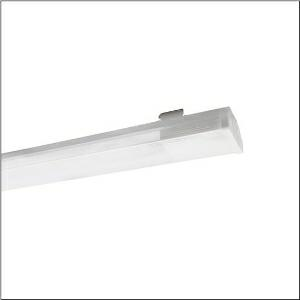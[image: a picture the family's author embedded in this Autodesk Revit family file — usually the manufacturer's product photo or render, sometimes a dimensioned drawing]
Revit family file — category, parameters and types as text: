
# Revit family: modario_r__31_gen_2_53bm8117u4gxc2_3746
name_source: partatom
category: Lighting Fixtures
units: mm (PartAtom-declared; Revit-internal decimal feet)

## family parameters
Cut with Voids When Loaded = No
Host = Face
Light Source = No
Part Type = Normal
Room Calculation Point = No
Round Connector Dimension = Use Diameter
Shared = No

## types (1)
- Modario® 31 Gen.2 (1 x LED, 16360 lm, 90.4 W, 4000K)
    Apparent Load = 90 VA
    CIE Flux Codes = 50 78 94 90 100
    Color Rendering = 80
    Color Temperature = 4000K
    Default Elevation = 1800 mm
    Description = Modario® 31 Gen.2, luminaire insert, of sheet steel, coil coated, white, length: 2.392mm, width: 81mm, height: 82mm, 8x system unit, system units: 299mm, LED rated luminous flux: 16.360lm, light colour: 840, control gear: ON/OFF, with plug, 3-pole, with phase selection, mains connection: 220..240V, AC, 50/60Hz, rated input power: 90W, through-wiring accessed according to module size, primary optical cover: cover, of PMMA, light emission: direct distribution, primary light characteristic: symmetric, protection rating (complete): IP20, protection rating (LED compartment): IP50, insulation class (complete): insulation class I (protective earthing), certification: CE, ENEC, VDE, UKCA, impact resistance: IK03, permissible ambient temperature for indoor applications: -40..+40°C, corresponds to IFS (International Featured Standards) requirements for safety and quality in the food industry, reducing of maximum allowable ambient temperature of 5°C with ceiling mounting, packaging unit: 1 piece
    Height = 92 mm
    Lamp = 1 x LED
    Lamp Light Flux = 16360 lm
    Lamp Power = 90.4 W
    Lamp count = 1
    Length = 2392 mm
    Luminous efficacy = 181 lm/W
    Manufacturer = Siteco
    ModVariant = No
    Model = 53BM8117U4GXC2
    Mounting Place = Ceiling
    Mounting Type = Pendant
    Number of Poles = 1
    OnlyDefault = Yes
    Power Factor = 1
    Product Name = Modario® 31 Gen.2
    Product group = luminaire insert | ceiling pendant
    ProductGroupID = 902
    Protection Class = Protection class I
    Protection Degree = IP 20
    RLX_Detail_Level = 1
    RLX_Emergency_Light_Flux = 0 lm
    RLX_Emergency_Type = 0
    RLX_Emergency_Type_DB = No
    RlxData = <blob elided: 34713 chars, md5=c2a42d41>
    Socket = socket
    Standby Power = 0 W
    System Light Flux = 16360 lm
    System Power = 90 W
    Type Comments = Product without accessories
    Type Image = l_1341883.jpg
    URL = http://relux.com
    VarID = ---
    Voltage = 0 V
    Weight = 0.00 kg
    Width = 81 mm

## geometry (parser evidence)
native form markers: Blend x4, Sweep x12
no freeform markers — native parametric forms only
